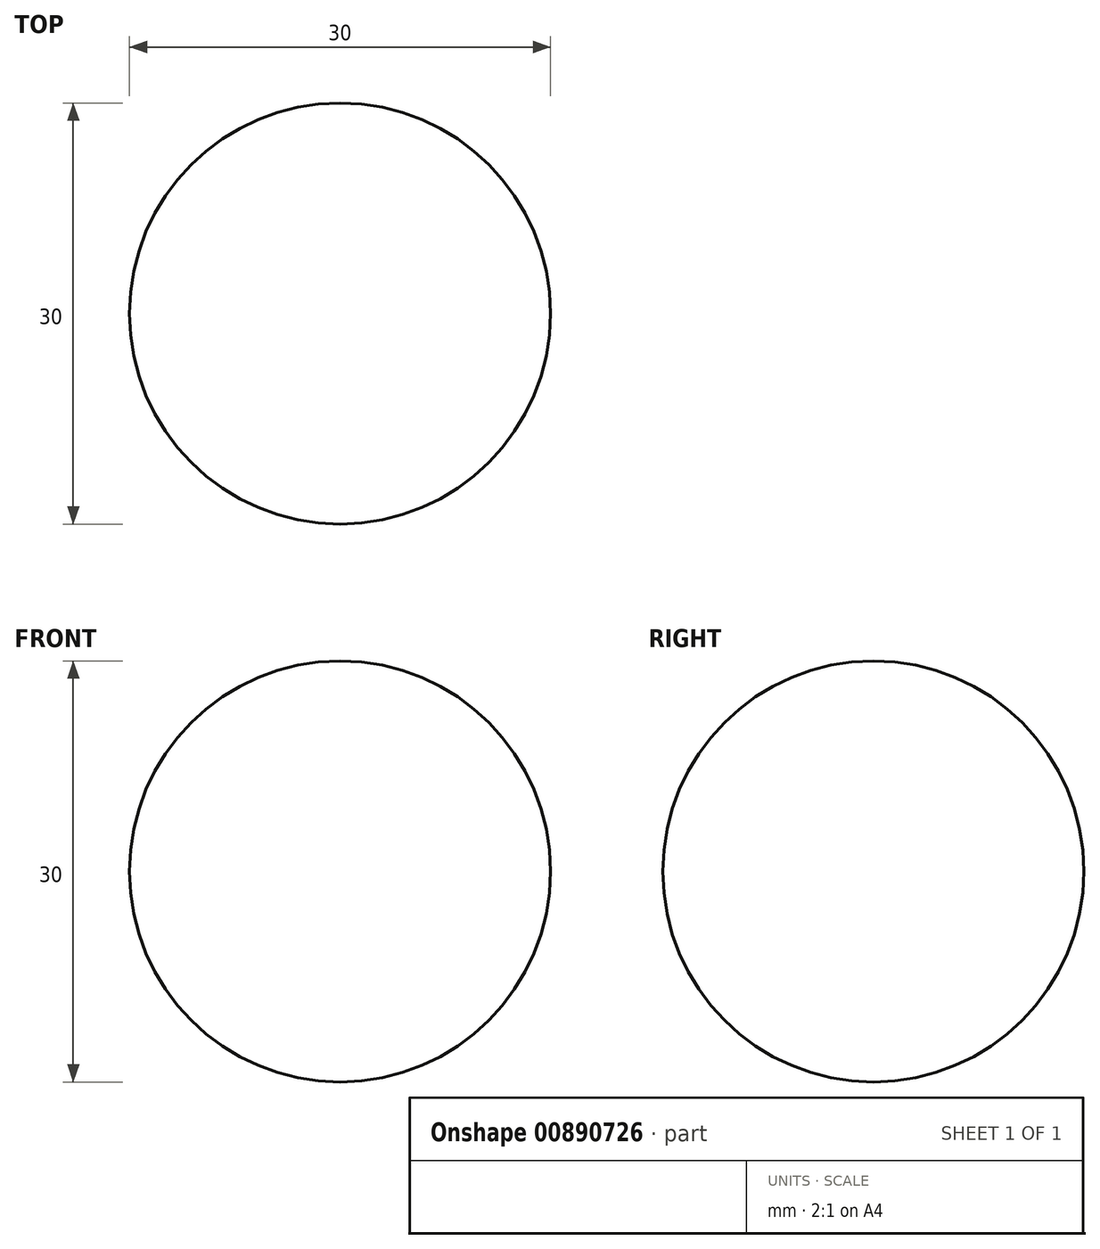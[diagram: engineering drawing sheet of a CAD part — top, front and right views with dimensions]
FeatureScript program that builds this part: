
annotation { "Feature Type Name" : "Feature", "Feature Type Description" : "" }
export const myFeature = defineFeature(function(context is Context, id is Id, definition is map)
    precondition{}
    {
        {
            var Q0;
            Q0=qCreatedBy(makeId("Top.planeOp"),FACE);
            var sketch = newSketch(context, id + "F0", { "sketchPlane" : qUnion([Q0])});
            skCircle(sketch, "E0", {"center": v(0, 0) * mm, "radius": 15 * mm});
            skLineSegment(sketch, "E1", {"start": v(0, 15) * mm, "end": v(0, -15) * mm});
            skSolve(sketch);
        }
        {
            var Q0;
            {var subQ0=sQuery(id+"F0.wireOp",EDGE,"E1");Q0=makeQuery(id+"F0.imprint","IMPRINT",FACE,{"disambiguationData":[TD([[makeQuery(id+"F0.imprint","IMPRINT",EDGE,{"derivedFrom":subQ0}),-1.0]])]});}
            var Q1;
            Q1=sQuery(id+"F0.wireOp",EDGE,"E1");
            revolve(context, id + "F1", {"surfaceOperationType" : NewSurfaceOperationType.NEW, "entities" : qUnion([Q0]), "axis" : qUnion([Q1]), "revolveType" : RevolveType.FULL});
        }
    });
